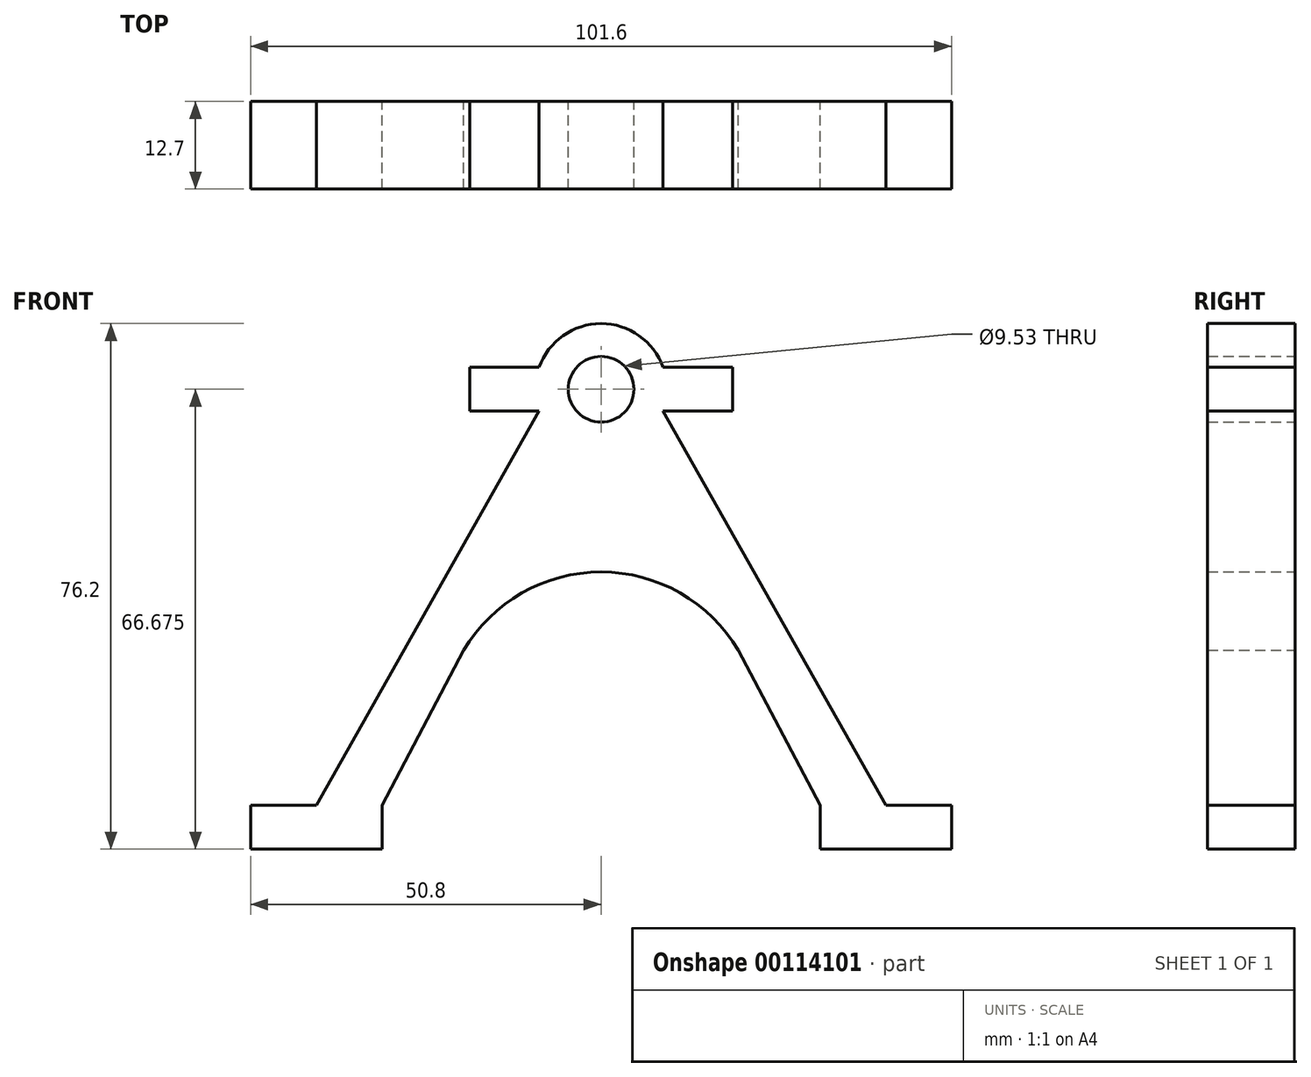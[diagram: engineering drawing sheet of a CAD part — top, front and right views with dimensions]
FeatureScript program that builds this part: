
annotation { "Feature Type Name" : "Feature", "Feature Type Description" : "" }
export const myFeature = defineFeature(function(context is Context, id is Id, definition is map)
    precondition{}
    {
        {
            var Q0;
            Q0=qCreatedBy(makeId("Front.planeOp"),FACE);
            var sketch = newSketch(context, id + "F0", { "sketchPlane" : qUnion([Q0])});
            skLineSegment(sketch, "E0.bottom", {"start": v(-50.8, 0) * mm, "end": v(-31.75, 0) * mm});
            skLineSegment(sketch, "E0.top", {"start": v(-50.8, 6.35) * mm, "end": v(-41.28, 6.35) * mm});
            skLineSegment(sketch, "E0.left", {"start": v(-50.8, 0) * mm, "end": v(-50.8, 6.35) * mm});
            skLineSegment(sketch, "E0.right", {"start": v(-31.75, 0) * mm, "end": v(-31.75, 6.35) * mm});
            skCircle(sketch, "E1", {"center": v(0, 66.68) * mm, "radius": 4.76 * mm});
            skLineSegment(sketch, "E2", {"start": v(-4.76, 66.68) * mm, "end": v(-9.53, 66.68) * mm});
            skLineSegment(sketch, "E3", {"start": v(4.76, 66.68) * mm, "end": v(9.53, 66.68) * mm});
            skLineSegment(sketch, "E4", {"start": v(-19.05, 63.5) * mm, "end": v(-8.98, 63.5) * mm});
            skLineSegment(sketch, "E5", {"start": v(-19.05, 69.85) * mm, "end": v(-8.98, 69.85) * mm});
            skLineSegment(sketch, "E6", {"start": v(-9.53, 66.68) * mm, "end": v(-19.05, 66.68) * mm});
            skLineSegment(sketch, "E7", {"start": v(9.53, 66.68) * mm, "end": v(19.05, 66.68) * mm});
            skLineSegment(sketch, "E8.trimOffspring", {"start": v(8.98, 69.85) * mm, "end": v(19.05, 69.85) * mm});
            skLineSegment(sketch, "E9.trimOffspring", {"start": v(8.98, 63.5) * mm, "end": v(19.05, 63.5) * mm});
            skLineSegment(sketch, "E10", {"start": v(-19.05, 69.85) * mm, "end": v(-19.05, 63.5) * mm});
            skLineSegment(sketch, "E11", {"start": v(19.05, 69.85) * mm, "end": v(19.05, 63.5) * mm});
            skArc(sketch, "E12.trimOffspring", {"start": v(8.98, 69.85) * mm, "mid": v(0, 76.2) * mm, "end": v(-8.98, 69.85) * mm});
            skPoint(sketch, "E13", {"position": v(-41.28, 6.35) * mm});
            skLineSegment(sketch, "E14", {"start": v(-41.28, 6.35) * mm, "end": v(-8.98, 63.5) * mm});
            skLineSegment(sketch, "E15", {"start": v(-31.75, 6.35) * mm, "end": v(-19.92, 28.83) * mm});
            skLineSegment(sketch, "E16.MirrorCS", {"start": v(41.28, 6.35) * mm, "end": v(8.98, 63.5) * mm});
            skLineSegment(sketch, "E17.MirrorCS", {"start": v(31.75, 6.35) * mm, "end": v(19.92, 28.83) * mm});
            skLineSegment(sketch, "E18.MirrorCS", {"start": v(50.8, 6.35) * mm, "end": v(41.28, 6.35) * mm});
            skLineSegment(sketch, "E19.MirrorCS", {"start": v(50.8, 0) * mm, "end": v(31.75, 0) * mm});
            skLineSegment(sketch, "E20.MirrorCS", {"start": v(31.75, 0) * mm, "end": v(31.75, 6.35) * mm});
            skLineSegment(sketch, "E21.MirrorCS", {"start": v(50.8, 0) * mm, "end": v(50.8, 6.35) * mm});
            skPoint(sketch, "E22.orphan", {"position": v(31.75, 6.35) * mm});
            skPoint(sketch, "E23", {"position": v(-19.92, 28.83) * mm});
            skPoint(sketch, "E24.MirrorP", {"position": v(19.92, 28.83) * mm});
            skArc(sketch, "E25", {"start": v(19.92, 28.83) * mm, "mid": v(0, 40.2) * mm, "end": v(-19.92, 28.83) * mm});
            skPoint(sketch, "E26.end.orphan", {"position": v(4.44, 58.25) * mm});
            skPoint(sketch, "E27.orphan", {"position": v(-4.44, 58.25) * mm});
            skSolve(sketch);
        }
        {
            var Q0;
            Q0=makeQuery(id+"F0.imprint","IMPRINT",FACE,{"disambiguationData":[TD([[makeQuery(id+"F0.imprint","IMPRINT",EDGE,{"derivedFrom":sQuery(id+"F0.wireOp",EDGE,"E0.bottom")}),1.0]])]});
            extrude(context, id + "F1", {"entities" : qUnion([Q0]), "depth" : 12.7 * mm});
        }
        {
            var Q0;
            {var subQ4=sQuery(id+"F0.wireOp",EDGE,"E2");Q0=makeQuery(id+"F0.imprint","IMPRINT",FACE,{"disambiguationData":[TD([[makeQuery(id+"F0.imprint","IMPRINT",EDGE,{"derivedFrom":subQ4}),-1.0]])]});}
            extrude(context, id + "F2", {"entities" : qUnion([Q0]), "operationType" : NewBodyOperationType.ADD, "depth" : 12.7 * mm});
        }
    });
